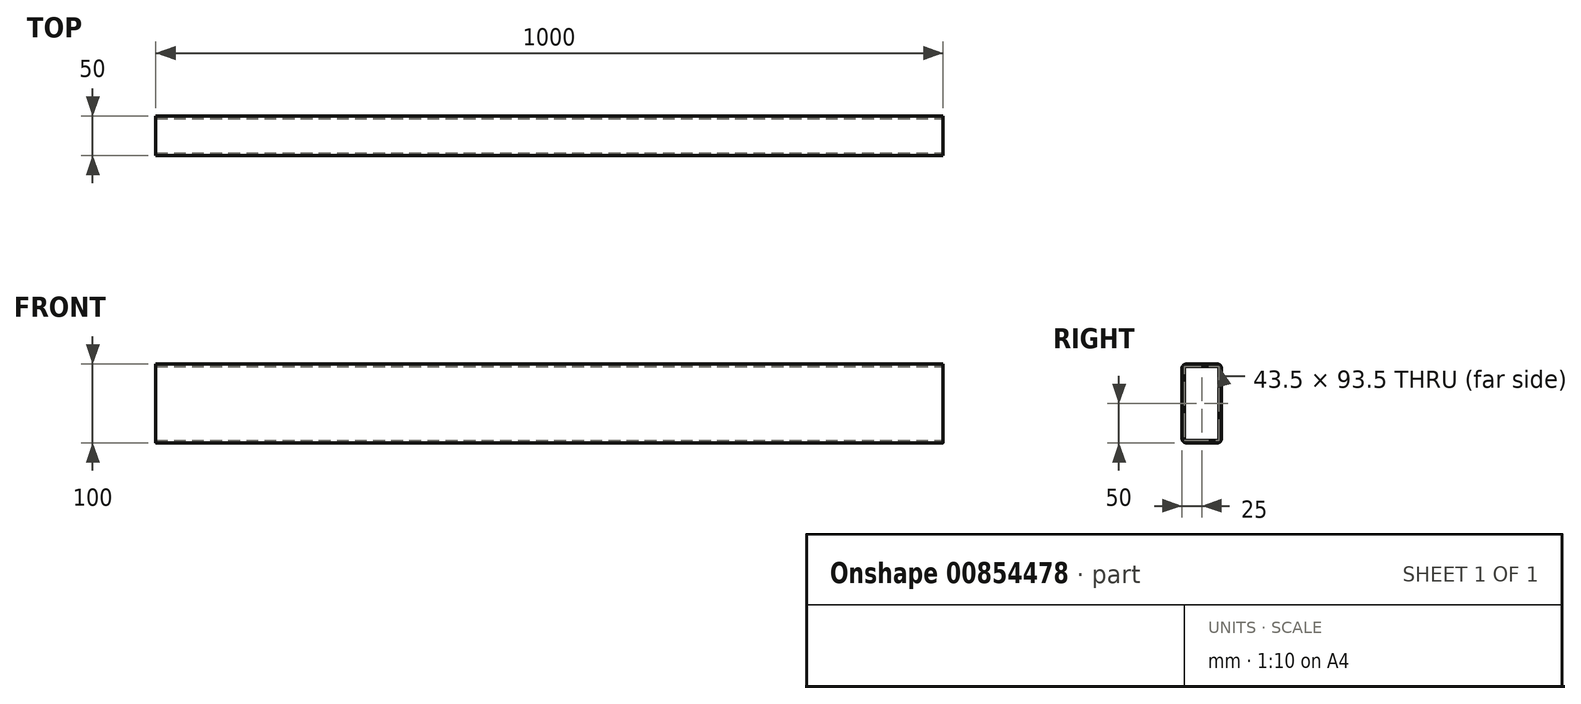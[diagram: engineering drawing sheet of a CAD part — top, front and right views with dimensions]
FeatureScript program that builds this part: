
annotation { "Feature Type Name" : "Feature", "Feature Type Description" : "" }
export const myFeature = defineFeature(function(context is Context, id is Id, definition is map)
    precondition{}
    {
        {
            var Q0;
            Q0=qCreatedBy(makeId("Front.planeOp"),FACE);
            var sketch = newSketch(context, id + "F0", { "sketchPlane" : qUnion([Q0])});
            skLineSegment(sketch, "E0.bottom", {"start": v(-500.77, 52.34) * mm, "end": v(499.23, 52.34) * mm});
            skLineSegment(sketch, "E0.top", {"start": v(-500.77, -47.66) * mm, "end": v(499.23, -47.66) * mm});
            skLineSegment(sketch, "E0.left", {"start": v(-500.77, 52.34) * mm, "end": v(-500.77, -47.66) * mm});
            skLineSegment(sketch, "E0.right", {"start": v(499.23, 52.34) * mm, "end": v(499.23, -47.66) * mm});
            skSolve(sketch);
        }
        {
            var Q0;
            Q0=makeQuery(id+"F0.imprint","IMPRINT",FACE,{"disambiguationData":[TD([[makeQuery(id+"F0.imprint","IMPRINT",EDGE,{"derivedFrom":sQuery(id+"F0.wireOp",EDGE,"E0.bottom")}),-1.0]])]});
            extrude(context, id + "F1", {"entities" : qUnion([Q0]), "depth" : 50 * mm, "offsetDistance" : 25 * mm});
        }
        {
            var Q0;
            Q0=makeQuery(id+"F1.opExtrude","SWEPT_FACE",FACE,{"disambiguationData":[OSD([sQuery(id+"F0.wireOp",EDGE,"E0.right")])]});
            var sketch = newSketch(context, id + "F2", { "sketchPlane" : qUnion([Q0])});
            skLineSegment(sketch, "E1.bottom", {"start": v(-46.75, 49.09) * mm, "end": v(-3.25, 49.09) * mm});
            skLineSegment(sketch, "E1.top", {"start": v(-46.75, -44.41) * mm, "end": v(-3.25, -44.41) * mm});
            skLineSegment(sketch, "E1.left", {"start": v(-46.75, 49.09) * mm, "end": v(-46.75, -44.41) * mm});
            skLineSegment(sketch, "E1.right", {"start": v(-3.25, 49.09) * mm, "end": v(-3.25, -44.41) * mm});
            skSolve(sketch);
        }
        {
            var Q0;
            Q0=makeQuery(id+"F2.imprint","IMPRINT",FACE,{"disambiguationData":[TD([[makeQuery(id+"F2.imprint","IMPRINT",EDGE,{"derivedFrom":sQuery(id+"F2.wireOp",EDGE,"E1.bottom")}),-1.0]])]});
            extrude(context, id + "F3", {"entities" : qUnion([Q0]), "operationType" : NewBodyOperationType.REMOVE, "endBound" : BoundingType.UP_TO_NEXT, "oppositeDirection" : true, "depth" : 188 * mm, "offsetDistance" : 25 * mm});
        }
        {
            var Q0;
            Q0=makeQuery(id+"F1.opExtrude","CAP_EDGE",EDGE,{"disambiguationData":[OSD([sQuery(id+"F0.wireOp",EDGE,"E0.bottom")])],"isStart":false});
            var Q1;
            Q1=makeQuery(id+"F1.opExtrude","CAP_EDGE",EDGE,{"disambiguationData":[OSD([sQuery(id+"F0.wireOp",EDGE,"E0.bottom")])],"isStart":true});
            var Q2;
            Q2=makeQuery(id+"F1.opExtrude","CAP_EDGE",EDGE,{"disambiguationData":[OSD([sQuery(id+"F0.wireOp",EDGE,"E0.top")])],"isStart":false});
            var Q3;
            Q3=makeQuery(id+"F1.opExtrude","CAP_EDGE",EDGE,{"disambiguationData":[OSD([sQuery(id+"F0.wireOp",EDGE,"E0.top")])],"isStart":true});
            fillet(context, id + "F4", {"entities" : qUnion([Q0, Q1, Q2, Q3]), "radius" : 5 * mm, "tangentPropagation" : true, "allowEdgeOverflow" : false});
        }
    });
